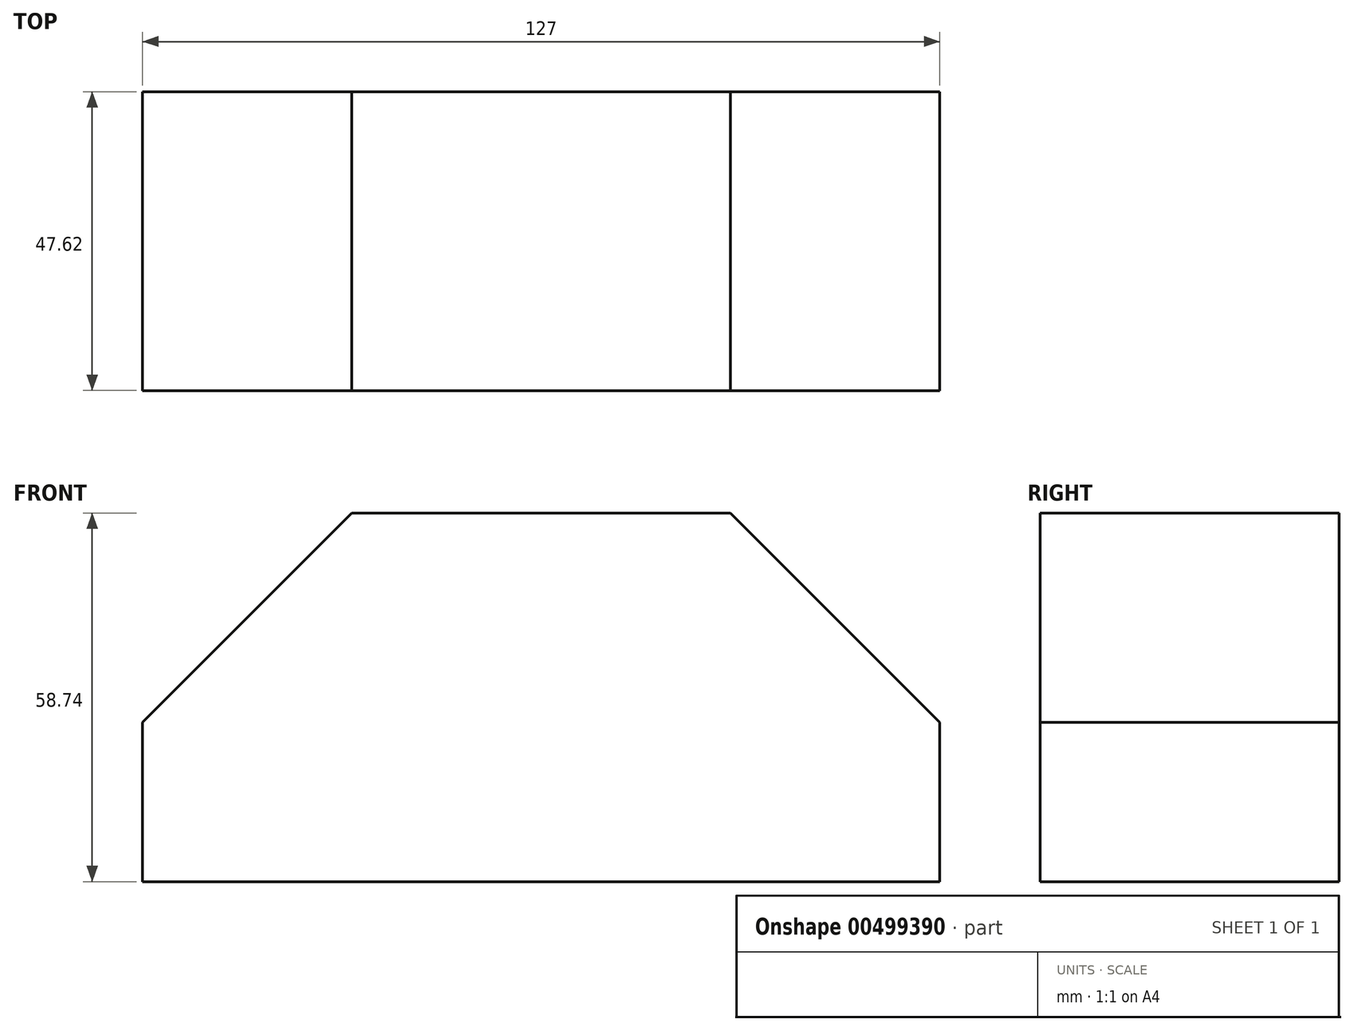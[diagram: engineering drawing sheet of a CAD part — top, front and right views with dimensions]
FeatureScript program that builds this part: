
annotation { "Feature Type Name" : "Feature", "Feature Type Description" : "" }
export const myFeature = defineFeature(function(context is Context, id is Id, definition is map)
    precondition{}
    {
        {
            var Q0;
            Q0=qCreatedBy(makeId("Front.planeOp"),FACE);
            var sketch = newSketch(context, id + "F0", { "sketchPlane" : qUnion([Q0])});
            skLineSegment(sketch, "E0.bottom", {"start": v(-60.64, 9.28) * mm, "end": v(66.36, 9.28) * mm});
            skLineSegment(sketch, "E0.top", {"start": v(-60.64, -49.46) * mm, "end": v(66.36, -49.46) * mm});
            skLineSegment(sketch, "E0.left", {"start": v(-60.64, 9.28) * mm, "end": v(-60.64, -49.46) * mm});
            skLineSegment(sketch, "E0.right", {"start": v(66.36, 9.28) * mm, "end": v(66.36, -49.46) * mm});
            skSolve(sketch);
        }
        {
            var Q0;
            Q0=makeQuery(id+"F0.imprint","IMPRINT",FACE,{"disambiguationData":[TD([[makeQuery(id+"F0.imprint","IMPRINT",EDGE,{"derivedFrom":sQuery(id+"F0.wireOp",EDGE,"E0.bottom")}),-1.0]])]});
            extrude(context, id + "F1", {"entities" : qUnion([Q0]), "depth" : 47.62 * mm});
        }
        {
            var Q0;
            Q0=makeQuery(id+"F1.opExtrude","CAP_FACE",FACE,{"disambiguationData":[OSD([sQuery(id+"F0.wireOp",EDGE,"E0.bottom"),sQuery(id+"F0.wireOp",EDGE,"E0.top"),sQuery(id+"F0.wireOp",EDGE,"E0.left"),sQuery(id+"F0.wireOp",EDGE,"E0.right")])],"isStart":false});
            var sketch = newSketch(context, id + "F2", { "sketchPlane" : qUnion([Q0])});
            skLineSegment(sketch, "E1", {"start": v(-60.64, -24.06) * mm, "end": v(-27.3, 9.28) * mm});
            skLineSegment(sketch, "E2", {"start": v(-27.3, 9.28) * mm, "end": v(-60.64, 9.28) * mm});
            skLineSegment(sketch, "E3", {"start": v(-60.64, 9.28) * mm, "end": v(-60.64, -24.06) * mm});
            skLineSegment(sketch, "E4", {"start": v(66.36, 9.28) * mm, "end": v(33.02, 9.28) * mm});
            skLineSegment(sketch, "E5", {"start": v(-60.64, -24.06) * mm, "end": v(66.36, -24.06) * mm});
            skLineSegment(sketch, "E6", {"start": v(33.02, 9.28) * mm, "end": v(66.36, -24.06) * mm});
            skLineSegment(sketch, "E7", {"start": v(66.36, 9.28) * mm, "end": v(66.36, -24.06) * mm});
            skSolve(sketch);
        }
        {
            var Q0;
            Q0=makeQuery(id+"F2.imprint","IMPRINT",FACE,{"disambiguationData":[TD([[makeQuery(id+"F2.imprint","IMPRINT",EDGE,{"derivedFrom":sQuery(id+"F2.wireOp",EDGE,"E1")}),1.0]])]});
            var Q1;
            Q1=makeQuery(id+"F2.imprint","IMPRINT",FACE,{"disambiguationData":[TD([[makeQuery(id+"F2.imprint","IMPRINT",EDGE,{"derivedFrom":sQuery(id+"F2.wireOp",EDGE,"E4")}),-1.0]])]});
            extrude(context, id + "F3", {"entities" : qUnion([Q0, Q1]), "operationType" : NewBodyOperationType.REMOVE, "oppositeDirection" : true, "depth" : 47.62 * mm});
        }
    });
